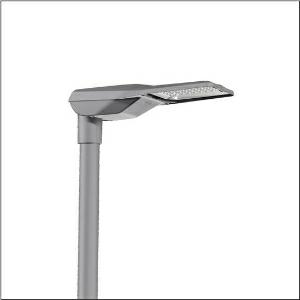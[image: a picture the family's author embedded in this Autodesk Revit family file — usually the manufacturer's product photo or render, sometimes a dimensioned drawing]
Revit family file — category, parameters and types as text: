
# Revit family: streetlight_sl_21_iq_mini___st0_8a_5xe2c41g08jb_e7d2
name_source: partatom
category: Lighting Fixtures
units: mm (PartAtom-declared; Revit-internal decimal feet)

## family parameters
Cut with Voids When Loaded = No
Host = Face
Light Source = No
Part Type = Normal
Room Calculation Point = No
Round Connector Dimension = Use Diameter
Shared = No

## types (1)
- --- (1 x LED, 11290 lm, 71.6 W, 4000K)
    Apparent Load = 72 VA
    CIE Flux Codes = 41 75 97 100 100
    Color Rendering = 70
    Color Temperature = 4000K
    Default Elevation = 1800 mm
    Description = Streetlight SL 21 iQ mini, mast luminaire, primary light control with lens, of PMMA, primary optical cover: cover, of toughened safety glass, transparent, light distribution: ST0.8a, light emission: direct distribution, primary light characteristic: asymmetric, installation type: post-top, side-entry, LED, High Power LED, rated luminous flux: 11.290lm, luminous efficacy: 158lm/W, light colour: 740, colour temperature: 4000K, control gear: iQ Street-Remote, control: Street-Remote, Auto-Match, Temp-Guard, Lumen-Switch, Night-Set, Smart-Wire, Light-Fading, Desk-Remote (wireless, voltage-free reading and setting of iQ features in the workshop via application-optimized NFC function/RFID function), optimised constant luminous flux control (CLO 2.0), pre-setting: linear dimming characteristic, mains connection: 220..240V, AC, 50/60Hz, start of lifetime: 72W, end of service life: 75W, reduction: 33W, luminaire housing, of diecast aluminium, powder-coated, SITECO metallic grey (DB 702S), corrosivity category C5 high according to DIN EN ISO 12944, please order mast flange separately, inclination adjustable: 0°, 5°, 10°, 15°, sealing non-destructively replaceable, multi-level sealing system, length: 628mm, width: 235mm, height: 110mm, mast flange for spigot size: 42mm (side-entry): 5XC10008XM4, 60/48mm (side-entry/post-top): 5XC10108XM2, 76/60mm (side-entry/post-top): 5XC10108XM1, mounting height: 4..8m, protection rating (complete): IP66, insulation class (complete): insulation class II (safety insulation), certification: CE, ENEC, ENEC+, VDE, impact resistance: IK10, permissible operating ambient temperature for outdoor applications: -40..+50°C, standard-compliant lighting for roads and squares, packaging unit: 1 piece

Light Distribution: ST0.8a
    Height = 110 mm
    Lamp = 1 x LED
    Lamp Light Flux = 11290 lm
    Lamp Power = 71.6 W
    Lamp count = 1
    Length = 625 mm
    Luminous efficacy = 158 lm/W
    Manufacturer = Siteco
    ModVariant = No
    Model = 5XE2C41G08JB
    Number of Poles = 1
    OnlyDefault = Yes
    Power Factor = 1
    Product Name = Streetlight SL 21 iQ mini | ST0.8a
    Product group = mast luminaire | pylon top
    ProductGroupID = 6100
    Protection Class = Protection class II
    Protection Degree = IP 66
    RLX_Detail_Level = 1
    RLX_Emergency_Light_Flux = 0 lm
    RLX_Emergency_Type = 0
    RLX_Emergency_Type_DB = No
    RlxData = <blob elided: 26353 chars, md5=9f020a36>
    Socket = socket
    Standby Power = 0 W
    System Light Flux = 11290 lm
    System Power = 72 W
    Type Comments = factory setting: luminous flux: 100 % | dim-lin: 254 | 746 mA
    Type Image = l_1003519.jpg
    URL = http://relux.com
    VarID = @adj_168669
    Voltage = 0 V
    Weight = 0.00 kg
    Width = 234 mm

## geometry (parser evidence)
native form markers: Blend x4, Sweep x10
no freeform markers — native parametric forms only
